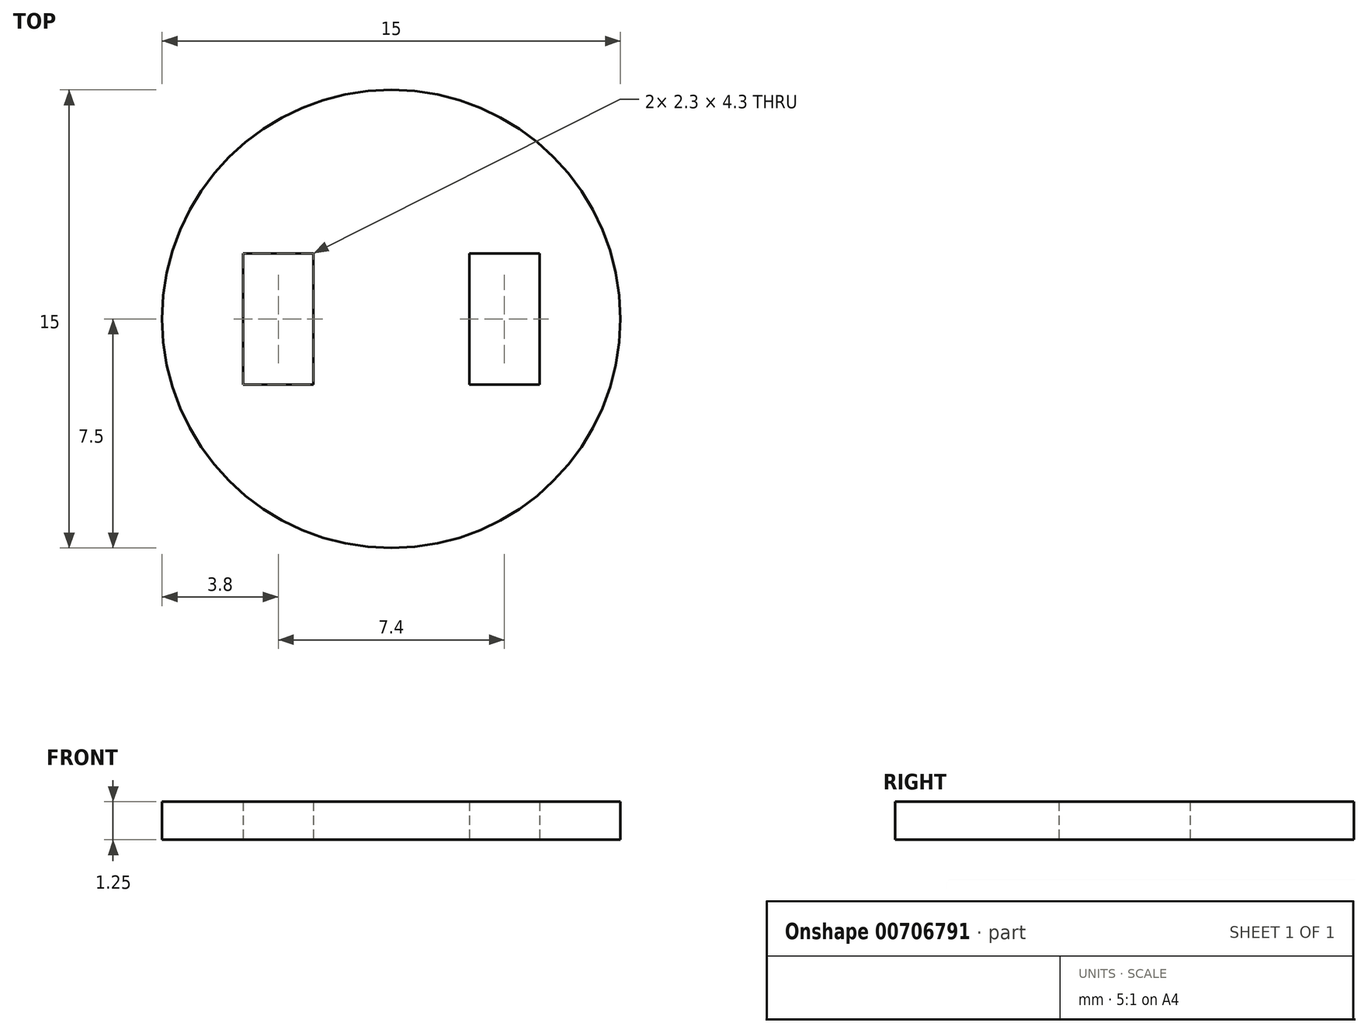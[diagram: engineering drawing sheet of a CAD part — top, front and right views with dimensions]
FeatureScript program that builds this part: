
annotation { "Feature Type Name" : "Feature", "Feature Type Description" : "" }
export const myFeature = defineFeature(function(context is Context, id is Id, definition is map)
    precondition{}
    {
        {
            var Q0;
            Q0=qCreatedBy(makeId("Top.planeOp"),FACE);
            var sketch = newSketch(context, id + "F0", { "sketchPlane" : qUnion([Q0])});
            skCircle(sketch, "E0", {"center": v(0, 0) * mm, "radius": 7.5 * mm});
            skLineSegment(sketch, "E1.bottom", {"start": v(-2.55, 2.15) * mm, "end": v(-4.85, 2.15) * mm});
            skLineSegment(sketch, "E1.top", {"start": v(-2.55, -2.15) * mm, "end": v(-4.85, -2.15) * mm});
            skLineSegment(sketch, "E1.left", {"start": v(-2.55, 2.15) * mm, "end": v(-2.55, -2.15) * mm});
            skLineSegment(sketch, "E1.right", {"start": v(-4.85, 2.15) * mm, "end": v(-4.85, -2.15) * mm});
            skPoint(sketch, "E1.middle", {"position": v(-3.7, 0) * mm});
            skLineSegment(sketch, "E2.bottom", {"start": v(2.55, 2.15) * mm, "end": v(4.85, 2.15) * mm});
            skLineSegment(sketch, "E2.top", {"start": v(2.55, -2.15) * mm, "end": v(4.85, -2.15) * mm});
            skLineSegment(sketch, "E2.left", {"start": v(2.55, 2.15) * mm, "end": v(2.55, -2.15) * mm});
            skLineSegment(sketch, "E2.right", {"start": v(4.85, 2.15) * mm, "end": v(4.85, -2.15) * mm});
            skPoint(sketch, "E2.middle", {"position": v(3.7, 0) * mm});
            skSolve(sketch);
        }
        {
            var Q0;
            Q0=makeQuery(id+"F0.imprint","IMPRINT",FACE,{"disambiguationData":[TD([[makeQuery(id+"F0.imprint","IMPRINT",EDGE,{"derivedFrom":sQuery(id+"F0.wireOp",EDGE,"E0")}),1.0]])]});
            extrude(context, id + "F1", {"entities" : qUnion([Q0]), "depth" : 1.25 * mm, "offsetDistance" : 25 * mm});
        }
    });
